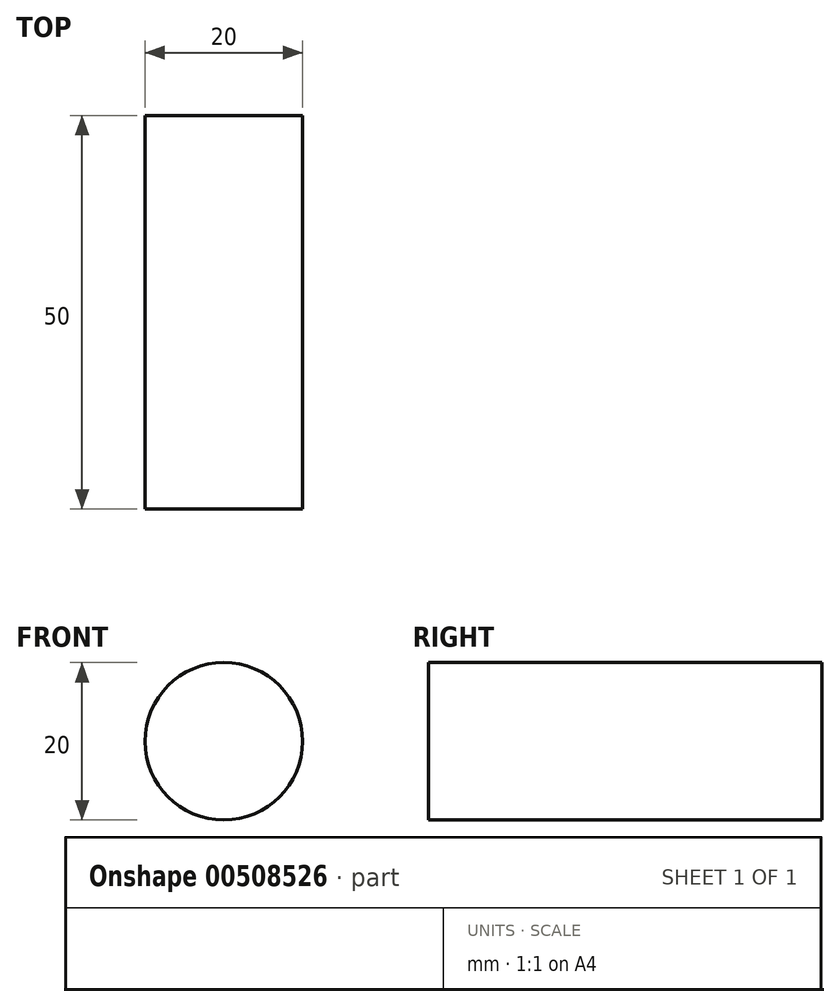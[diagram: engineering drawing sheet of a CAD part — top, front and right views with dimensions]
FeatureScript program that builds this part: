
annotation { "Feature Type Name" : "Feature", "Feature Type Description" : "" }
export const myFeature = defineFeature(function(context is Context, id is Id, definition is map)
    precondition{}
    {
        {
            var Q0;
            Q0=qCreatedBy(makeId("Front.planeOp"),FACE);
            var sketch = newSketch(context, id + "F0", { "sketchPlane" : qUnion([Q0])});
            skCircle(sketch, "E0", {"center": v(0, 0) * mm, "radius": 10 * mm});
            skSolve(sketch);
        }
        {
            var Q0;
            Q0=qSketchRegion(id+"F0",true);
            extrude(context, id + "F1", {"entities" : qUnion([Q0]), "depth" : 50 * mm});
        }
    });
